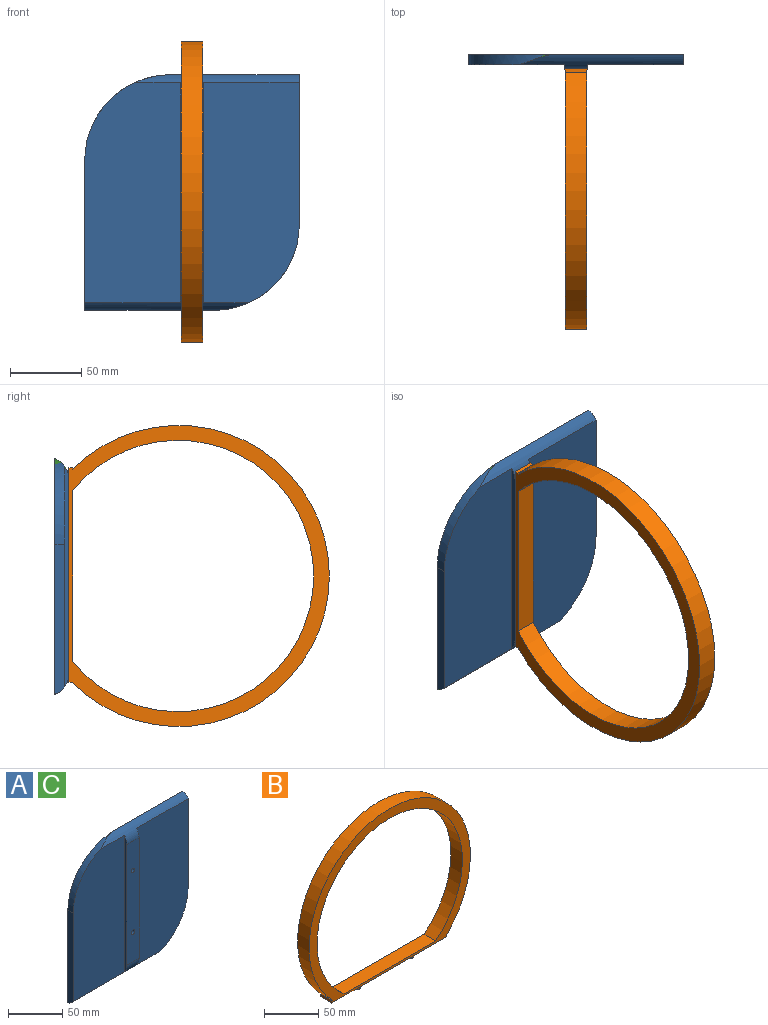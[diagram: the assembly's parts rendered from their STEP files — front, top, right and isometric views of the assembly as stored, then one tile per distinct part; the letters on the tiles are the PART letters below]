
ASSEMBLY  parts=3 mates=1
PART A: 16 faces, bbox 150.3x10x164.8 mm
  f0: cylinder r=60mm len=60mm, axis (0,-1,0), area 558.9mm2, adj f1,f4,f5,f15
  f1: plane 104.83x7mm, normal (-1,0,0), area 719.6mm2, adj f0,f4,f5,f14
  f2: cylinder r=60mm len=60mm, axis (0,-1,0), area 558.9mm2, adj f3,f4,f13,f14
  f3: plane 104.83x7mm, normal (1,0,0), area 719.6mm2, adj f2,f4,f13,f15
  f4: plane 164.83x150.25mm, normal (0,1,0), area 23221.1mm2, adj f0,f1,f2,f3,f14,f15
  f5: plane 154.55x67.05mm, normal (0,-1,0), area 9814.7mm2, adj f0,f1,f7,f14,f15
  f6: plane 154.55x3mm, normal (1,0,0), area 446.4mm2, adj f8,f13,f14,f15
  f7: plane 154.55x3mm, normal (-1,0,0), area 446.4mm2, adj f5,f8,f14,f15
  f8: plane 136.55x16mm, normal (0,-1,0), area 2145.5mm2, adj f6,f7,f9,f11,f14,f15
  f9: cylinder r=2.5mm len=7mm, axis (0,1,0), area 110mm2, adj f8,f10
  f10: plane 5x5mm, normal (0,-1,0), area 19.6mm2, adj f9
  f11: cylinder r=2.5mm len=7mm, axis (0,1,0), area 110mm2, adj f8,f12
  f12: plane 5x5mm, normal (0,-1,0), area 19.6mm2, adj f11
  f13: plane 154.55x67.2mm, normal (0,-1,0), area 9837.4mm2, adj f2,f3,f6,f14,f15
  f14: cylinder r=15mm len=114.55mm, axis (-1,0,0), area 1081.4mm2, adj f1,f2,f4,f5,f6,f7,f8,f13
  f15: cylinder r=15mm len=114.55mm, axis (-1,0,0), area 1081.4mm2, adj f0,f3,f4,f5,f6,f7,f8,f13
PART B: 14 faces, bbox 210.9x15x189.3 mm
  f0: plane 150x15mm, normal (0,0,-1), area 2210.7mm2, adj f2,f5,f6,f8,f10,f12
  f1: plane 15x0.93mm, normal (0,0,1), area 14mm2, adj f4,f5,f6,f8
  f2: plane 15x2.5mm, normal (1,0,0), area 37.5mm2, adj f0,f3,f5,f6
  f3: plane 15x0.4mm, normal (0,0,-1), area 5.9mm2, adj f2,f4,f5,f6
  f4: cylinder r=105.43mm len=210.85mm, axis (0,-1,0), area 7444.3mm2, adj f1,f3,f5,f6
  f5: plane 210.85x182.29mm, normal (0,-1,0), area 5464.8mm2, adj f0,f1,f2,f3,f4,f7,f8,f9
  f6: plane 210.85x182.29mm, normal (0,1,0), area 5464.8mm2, adj f0,f1,f2,f3,f4,f7,f8,f9
  f7: cylinder r=95mm len=190mm, axis (0,1,0), area 7015.6mm2, adj f5,f6,f9
  f8: plane 15x2.5mm, normal (-1,0,0), area 37.5mm2, adj f0,f1,f5,f6
  f9: plane 119.47x15mm, normal (0,0,1), area 1792mm2, adj f5,f6,f7
  f10: cylinder r=2.5mm len=7mm, axis (0,0,-1), area 110mm2, adj f0,f11
  f11: plane 5x5mm, normal (0,0,-1), area 19.6mm2, adj f10
  f12: cylinder r=2.5mm len=7mm, axis (0,0,-1), area 110mm2, adj f0,f13
  f13: plane 5x5mm, normal (0,0,-1), area 19.6mm2, adj f12
PART C: same geometry as A
PLACE A t=(-50.15,12.95,-33.21)mm
PLACE B rot(axis=(0.58,0.58,-0.58),120deg) t=(-42.65,0.45,-5.62)mm
PLACE C t=(-50.15,12.95,-33.21)mm
MATE fastened B.f10 <-> A.f9  axis (0,1,0) through (-50.15,9.95,29.38)mm
